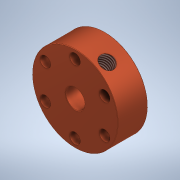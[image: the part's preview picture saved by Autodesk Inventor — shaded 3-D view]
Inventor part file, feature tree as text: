
AUTODESK INVENTOR PART (.ipt)
format: ipt  version: 2020 (Build 240168000, 168)  size: 172,032 bytes
history: native  units: mm
features: sketch x3, hole x2, plane x2, revolve x1, pattern_circular x1, chamfer x1
ambient origin geometry x8: Origin, YZ Plane, XZ Plane, XY Plane, X Axis, Y Axis, Z Axis, Center Point
bodies: Solid1 (feature_tree)
feature tree (10):
  revolve  "Revolution1"  [1 undecoded]
  hole  "Hole1"  [1 undecoded]
  pattern_circular  "Circular Pattern1"  [2 undecoded]
  plane  "Work Plane2"
  hole  "Hole2"  [1 undecoded]
  chamfer  "Chamfer1"  Angle=60.0deg  [1 undecoded]
  sketch  "Sketch1"  dims[d0=9.0mm d1=25.2mm]
  sketch  "Sketch2"  dims[d3=14.0mm d4=40.0mm]
  plane  "Work Plane1"
  sketch  "Sketch3"  dims[d5=90.0deg d6=16.0mm d7=5.0mm d8=6.0mm d9=4.0mm d10=2.0mm d11=90.0deg d12=8.0mm d13=20.594885mm d14=60.0mm d15=360.0deg d17=60.0deg d18=6.647mm d19=10.0mm d20=4.0mm d21=2.0mm d22=90.0deg d23=20.2mm d24=20.594885mm d25=0.2mm d26=2.0mm d27=45.0deg d28=2.0mm]
note: 6 required parameter values undecoded (feature->parameter linkage not recoverable at this tier; creation-order binding heuristic only, values carry confidence <= 0.55)